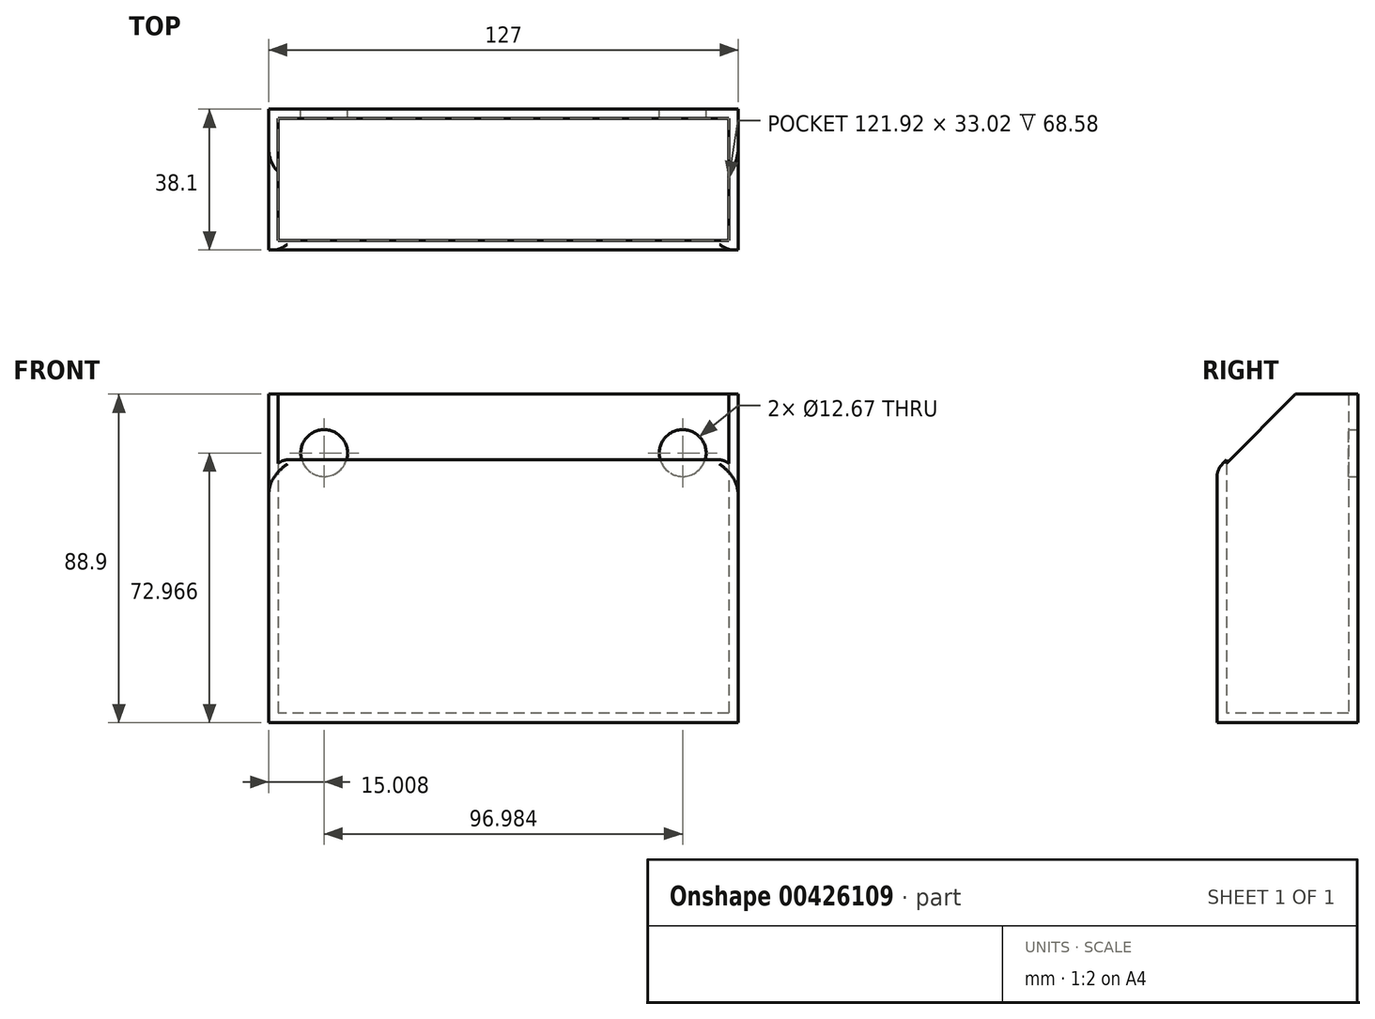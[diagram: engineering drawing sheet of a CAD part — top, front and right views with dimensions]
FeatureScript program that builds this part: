
annotation { "Feature Type Name" : "Feature", "Feature Type Description" : "" }
export const myFeature = defineFeature(function(context is Context, id is Id, definition is map)
    precondition{}
    {
        {
            var Q0;
            Q0=qCreatedBy(makeId("Front.planeOp"),FACE);
            var sketch = newSketch(context, id + "F0", { "sketchPlane" : qUnion([Q0])});
            skLineSegment(sketch, "E0.bottom", {"start": v(63.5, 44.45) * mm, "end": v(-63.5, 44.45) * mm});
            skLineSegment(sketch, "E0.top", {"start": v(63.5, -44.45) * mm, "end": v(-63.5, -44.45) * mm});
            skLineSegment(sketch, "E0.left", {"start": v(63.5, 44.45) * mm, "end": v(63.5, -44.45) * mm});
            skLineSegment(sketch, "E0.right", {"start": v(-63.5, 44.45) * mm, "end": v(-63.5, -44.45) * mm});
            skPoint(sketch, "E0.middle", {"position": v(0, 0) * mm});
            skSolve(sketch);
        }
        {
            var Q0;
            Q0 = qSketchRegion(id + "F0", true);
            extrude(context, id + "F1", {"entities" : qUnion([Q0]), "oppositeDirection" : true, "depth" : 38.1 * mm});
        }
        {
            var Q0;
            Q0=makeQuery(id+"F1.opExtrude","SWEPT_FACE",FACE,{"disambiguationData":[OSD([sQuery(id+"F0.wireOp",EDGE,"E0.bottom")])]});
            shell(context, id + "F2", {"entities" : qUnion([Q0]), "thickness" : 2.54 * mm});
        }
        {
            var Q0;
            Q0=makeQuery(id+"F1.opExtrude","CAP_EDGE",EDGE,{"disambiguationData":[OSD([sQuery(id+"F0.wireOp",EDGE,"E0.bottom")])],"isStart":true});
            chamfer(context, id + "F3", {"entities" : qUnion([Q0]), "chamferType" : ChamferType.OFFSET_ANGLE, "width" : 20.32 * mm, "oppositeDirection" : false, "angle" : 45 * degree, "tangentPropagation" : true});
        }
        {
            var Q0;
            Q0=makeQuery(id+"F3.opChamfer","BLEND_EDGE",EDGE,{"blendedFrom":[makeQuery(id+"F1.opExtrude","CAP_EDGE",EDGE,{"disambiguationData":[OSD([sQuery(id+"F0.wireOp",EDGE,"E0.bottom")])],"isStart":true}),makeQuery(id+"F1.opExtrude","SWEPT_FACE",FACE,{"disambiguationData":[OSD([sQuery(id+"F0.wireOp",EDGE,"E0.right")])]})],"blendedInto":[makeQuery(id+"F1.opExtrude","SWEPT_FACE",FACE,{"disambiguationData":[OSD([sQuery(id+"F0.wireOp",EDGE,"E0.right")])]})]});
            var Q1;
            Q1=makeQuery(id+"F3.opChamfer","BLEND_EDGE",EDGE,{"blendedFrom":[makeQuery(id+"F1.opExtrude","CAP_EDGE",EDGE,{"disambiguationData":[OSD([sQuery(id+"F0.wireOp",EDGE,"E0.bottom")])],"isStart":true}),makeQuery(id+"F1.opExtrude","SWEPT_FACE",FACE,{"disambiguationData":[OSD([sQuery(id+"F0.wireOp",EDGE,"E0.left")])]})],"blendedInto":[makeQuery(id+"F1.opExtrude","SWEPT_FACE",FACE,{"disambiguationData":[OSD([sQuery(id+"F0.wireOp",EDGE,"E0.left")])]})]});
            var Q2;
            {var subQ0=sQuery(id+"F0.wireOp",EDGE,"E0.bottom");Q2=makeQuery(id+"F3.opChamfer","BLEND_EDGE",EDGE,{"blendedFrom":[makeQuery(id+"F1.opExtrude","CAP_EDGE",EDGE,{"disambiguationData":[OSD([subQ0])],"isStart":true}),makeQuery(id+"F1.opExtrude","CAP_FACE",FACE,{"disambiguationData":[OSD([subQ0,sQuery(id+"F0.wireOp",EDGE,"E0.top"),sQuery(id+"F0.wireOp",EDGE,"E0.left"),sQuery(id+"F0.wireOp",EDGE,"E0.right")])],"isStart":true})],"blendedInto":[makeQuery(id+"F1.opExtrude","CAP_FACE",FACE,{"disambiguationData":[OSD([subQ0,sQuery(id+"F0.wireOp",EDGE,"E0.top"),sQuery(id+"F0.wireOp",EDGE,"E0.left"),sQuery(id+"F0.wireOp",EDGE,"E0.right")])],"isStart":true})]});}
            fillet(context, id + "F4", {"entities" : qUnion([Q0, Q1, Q2]), "radius" : 5.08 * mm, "tangentPropagation" : true, "allowEdgeOverflow" : false});
        }
        {
            var Q0;
            Q0=makeQuery(id+"F1.opExtrude","CAP_FACE",FACE,{"disambiguationData":[OSD([sQuery(id+"F0.wireOp",EDGE,"E0.bottom"),sQuery(id+"F0.wireOp",EDGE,"E0.top"),sQuery(id+"F0.wireOp",EDGE,"E0.left"),sQuery(id+"F0.wireOp",EDGE,"E0.right")])],"isStart":false});
            var sketch = newSketch(context, id + "F5", { "sketchPlane" : qUnion([Q0])});
            skCircle(sketch, "E1", {"center": v(-48.5, 28.52) * mm, "radius": 6.33 * mm});
            skLineSegment(sketch, "E2", {"start": v(0, 44.45) * mm, "end": v(0, -27.28) * mm, "construction": true});
            skCircle(sketch, "E3.MirrorC", {"center": v(48.5, 28.52) * mm, "radius": 6.33 * mm});
            skSolve(sketch);
        }
        {
            var Q0;
            Q0 = qSketchRegion(id + "F5", true);
            extrude(context, id + "F6", {"entities" : qUnion([Q0]), "operationType" : NewBodyOperationType.REMOVE, "oppositeDirection" : true, "depth" : 25.4 * mm});
        }
    });
